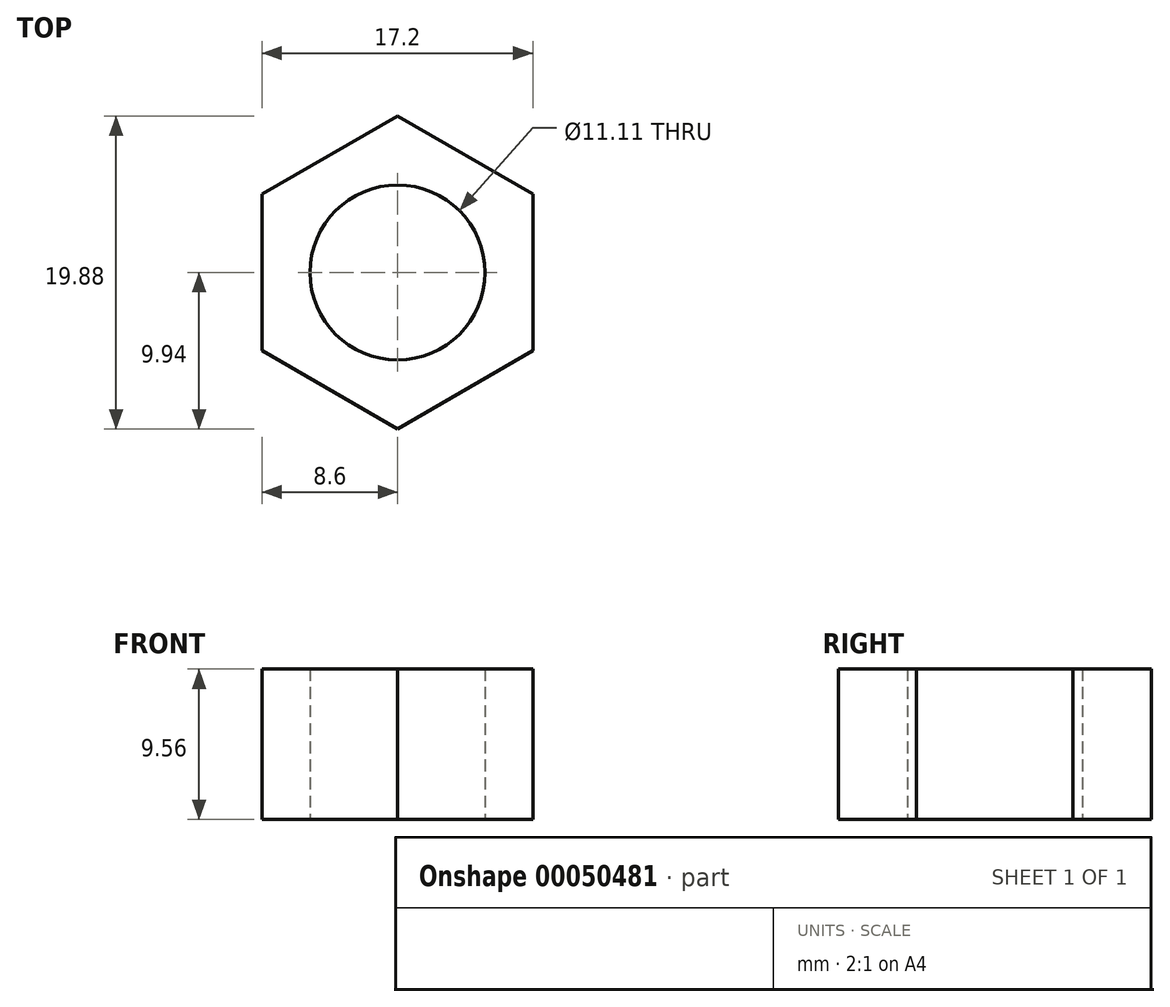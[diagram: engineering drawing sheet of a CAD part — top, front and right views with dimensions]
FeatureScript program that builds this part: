
annotation { "Feature Type Name" : "Feature", "Feature Type Description" : "" }
export const myFeature = defineFeature(function(context is Context, id is Id, definition is map)
    precondition{}
    {
        {
            var Q0;
            Q0=qCreatedBy(makeId("Top.planeOp"),FACE);
            var sketch = newSketch(context, id + "F0", { "sketchPlane" : qUnion([Q0])});
            skCircle(sketch, "E0", {"center": v(0, 0) * mm, "radius": 5.56 * mm});
            skCircle(sketch, "E1.cCircle", {"center": v(0, 0) * mm, "radius": 8.6 * mm, "construction": true});
            skLineSegment(sketch, "E1.0", {"start": v(8.6, 4.97) * mm, "end": v(8.6, -4.97) * mm});
            skLineSegment(sketch, "E1.1", {"start": v(8.6, -4.97) * mm, "end": v(0, -9.94) * mm});
            skLineSegment(sketch, "E1.2", {"start": v(0, -9.94) * mm, "end": v(-8.6, -4.97) * mm});
            skLineSegment(sketch, "E1.3", {"start": v(-8.6, -4.97) * mm, "end": v(-8.6, 4.97) * mm});
            skLineSegment(sketch, "E1.4", {"start": v(-8.6, 4.97) * mm, "end": v(0, 9.94) * mm});
            skLineSegment(sketch, "E1.5", {"start": v(0, 9.94) * mm, "end": v(8.6, 4.97) * mm});
            skPoint(sketch, "E1.0.midPoint", {"position": v(8.6, 0) * mm});
            skSolve(sketch);
        }
        {
            var Q0;
            Q0=qSketchRegion(id+"F0",true);
            extrude(context, id + "F1", {"entities" : qUnion([Q0]), "endBound" : BoundingType.SYMMETRIC, "depth" : 9.56 * mm});
        }
    });
